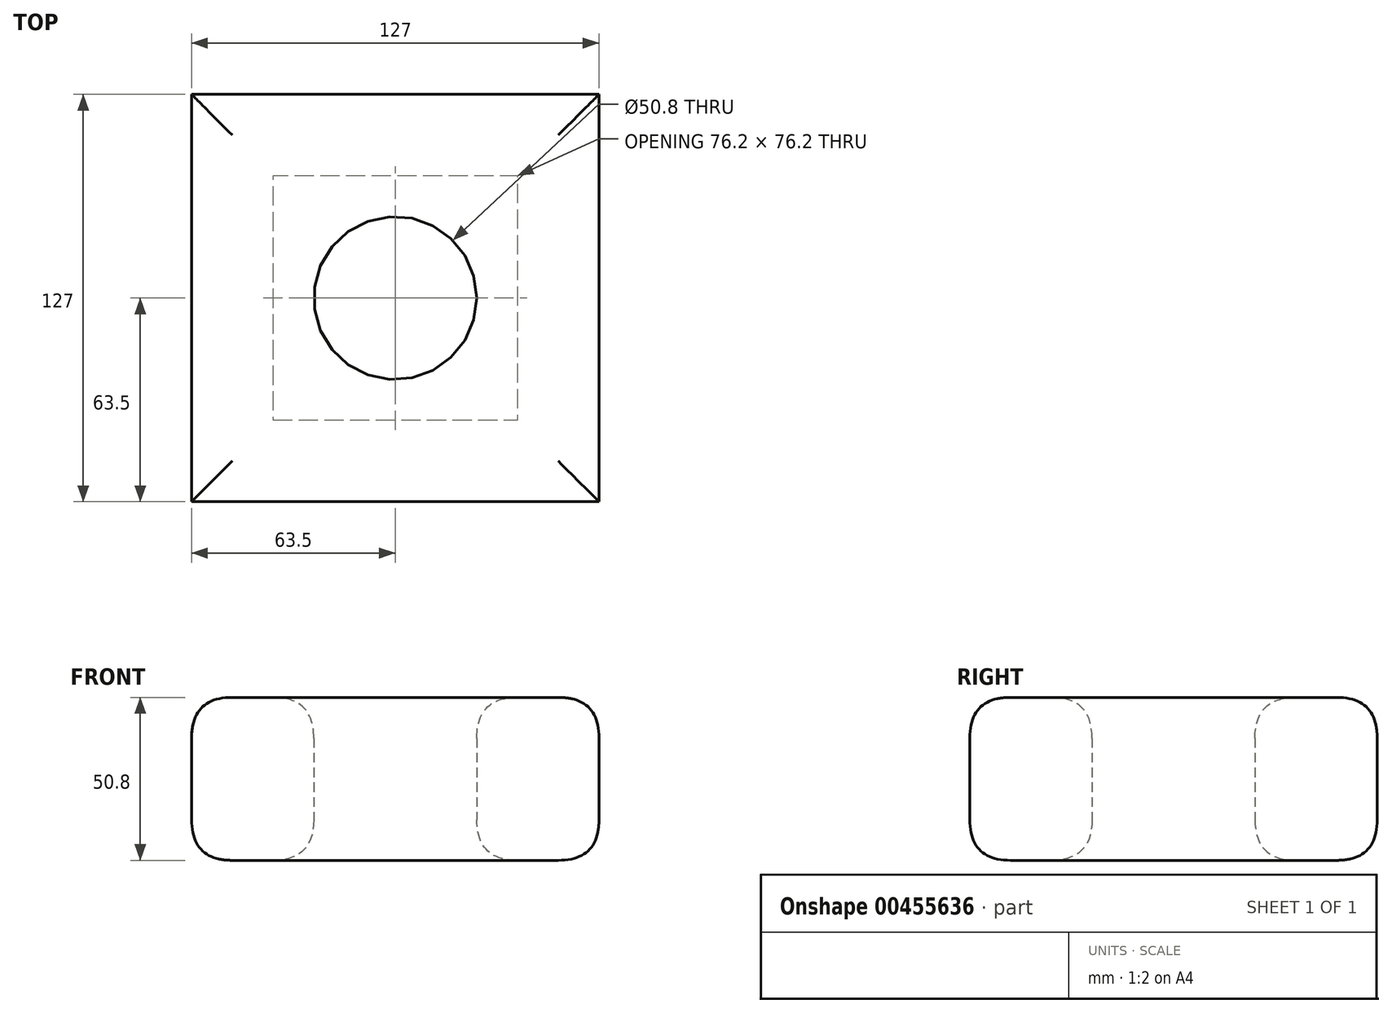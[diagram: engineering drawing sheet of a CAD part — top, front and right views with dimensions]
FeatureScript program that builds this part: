
annotation { "Feature Type Name" : "Feature", "Feature Type Description" : "" }
export const myFeature = defineFeature(function(context is Context, id is Id, definition is map)
    precondition{}
    {
        {
            var Q0;
            Q0=qCreatedBy(makeId("Top.planeOp"),FACE);
            var sketch = newSketch(context, id + "F0", { "sketchPlane" : qUnion([Q0])});
            skLineSegment(sketch, "E0.bottom", {"start": v(127, 0) * mm, "end": v(0, 0) * mm});
            skLineSegment(sketch, "E0.top", {"start": v(127, -127) * mm, "end": v(0, -127) * mm});
            skLineSegment(sketch, "E0.left", {"start": v(127, 0) * mm, "end": v(127, -127) * mm});
            skLineSegment(sketch, "E0.right", {"start": v(0, 0) * mm, "end": v(0, -127) * mm});
            skCircle(sketch, "E1", {"center": v(63.5, -63.5) * mm, "radius": 25.4 * mm});
            skSolve(sketch);
        }
        {
            var Q0;
            Q0=makeQuery(id+"F0.imprint","IMPRINT",FACE,{"disambiguationData":[TD([[makeQuery(id+"F0.imprint","IMPRINT",EDGE,{"derivedFrom":sQuery(id+"F0.wireOp",EDGE,"E0.bottom")}),1.0]])]});
            var Q1;
            Q1=sQuery(id+"F0.wireOp",EDGE,"E0.left");
            var Q2;
            Q2=sQuery(id+"F0.wireOp",EDGE,"E0.bottom");
            var Q3;
            Q3=sQuery(id+"F0.wireOp",EDGE,"E0.right");
            var Q4;
            Q4=sQuery(id+"F0.wireOp",EDGE,"E0.top");
            extrude(context, id + "F1", {"entities" : qUnion([Q0]), "surfaceEntities" : qUnion([Q1, Q2, Q3, Q4]), "depth" : 50.8 * mm});
        }
        {
            var Q0;
            Q0=makeQuery(id+"F1.opExtrude","CAP_EDGE",EDGE,{"disambiguationData":[OSD([sQuery(id+"F0.wireOp",EDGE,"E0.top")])],"isStart":false});
            var Q1;
            Q1=makeQuery(id+"F1.opExtrude","CAP_EDGE",EDGE,{"disambiguationData":[OSD([sQuery(id+"F0.wireOp",EDGE,"E0.right")])],"isStart":false});
            var Q2;
            Q2=makeQuery(id+"F1.opExtrude","CAP_EDGE",EDGE,{"disambiguationData":[OSD([sQuery(id+"F0.wireOp",EDGE,"E0.left")])],"isStart":false});
            var Q3;
            Q3=makeQuery(id+"F1.opExtrude","CAP_EDGE",EDGE,{"disambiguationData":[OSD([sQuery(id+"F0.wireOp",EDGE,"E0.bottom")])],"isStart":false});
            var Q4;
            Q4=makeQuery(id+"F1.opExtrude","CAP_EDGE",EDGE,{"disambiguationData":[OSD([sQuery(id+"F0.wireOp",EDGE,"E0.top")])],"isStart":true});
            var Q5;
            Q5=makeQuery(id+"F1.opExtrude","CAP_EDGE",EDGE,{"disambiguationData":[OSD([sQuery(id+"F0.wireOp",EDGE,"E0.right")])],"isStart":true});
            var Q6;
            Q6=makeQuery(id+"F1.opExtrude","CAP_EDGE",EDGE,{"disambiguationData":[OSD([sQuery(id+"F0.wireOp",EDGE,"E0.bottom")])],"isStart":true});
            var Q7;
            Q7=makeQuery(id+"F1.opExtrude","CAP_FACE",FACE,{"disambiguationData":[OSD([sQuery(id+"F0.wireOp",EDGE,"E0.bottom"),sQuery(id+"F0.wireOp",EDGE,"E0.top"),sQuery(id+"F0.wireOp",EDGE,"E0.left"),sQuery(id+"F0.wireOp",EDGE,"E0.right")])],"isStart":true});
            var Q8;
            Q8=makeQuery(id+"F1.opExtrude","CAP_EDGE",EDGE,{"disambiguationData":[OSD([sQuery(id+"F0.wireOp",EDGE,"E1")])],"isStart":false});
            var Q9;
            Q9=makeQuery(id+"F1.opExtrude","CAP_EDGE",EDGE,{"disambiguationData":[OSD([sQuery(id+"F0.wireOp",EDGE,"E1")])],"isStart":true});
            fillet(context, id + "F2", {"entities" : qUnion([Q0, Q1, Q2, Q3, Q4, Q5, Q6, Q7, Q8, Q9]), "radius" : 12.7 * mm, "tangentPropagation" : true, "rho" : 0.5, "crossSection" : FilletCrossSection.CONIC, "allowEdgeOverflow" : false});
        }
    });
